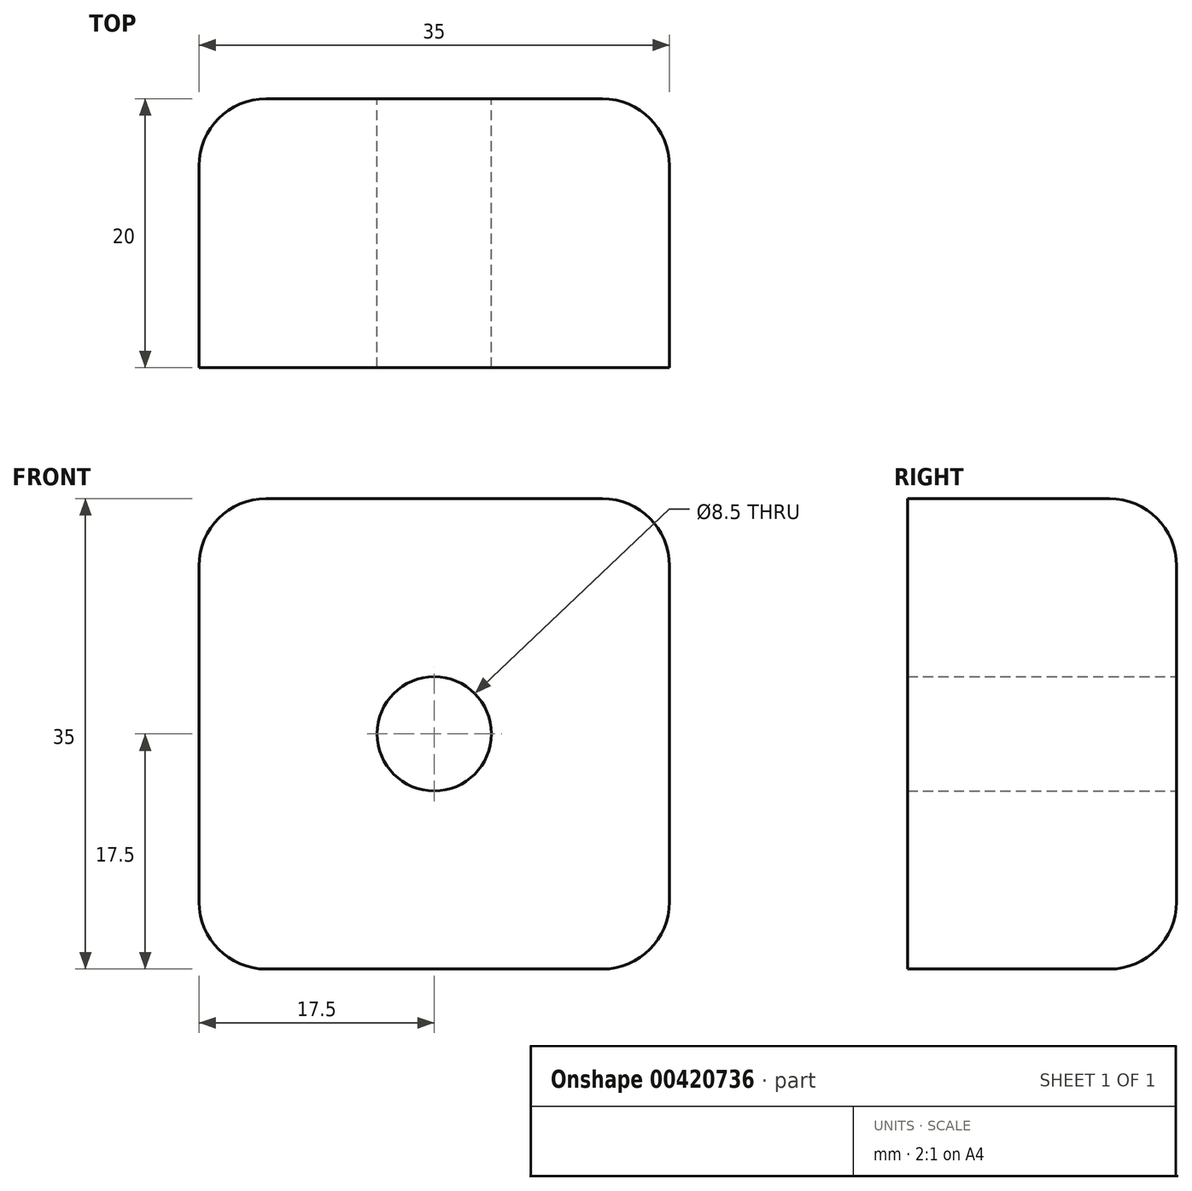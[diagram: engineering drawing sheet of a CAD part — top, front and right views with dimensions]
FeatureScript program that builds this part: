
annotation { "Feature Type Name" : "Feature", "Feature Type Description" : "" }
export const myFeature = defineFeature(function(context is Context, id is Id, definition is map)
    precondition{}
    {
        {
            var Q0;
            Q0=qCreatedBy(makeId("Front.planeOp"),FACE);
            var sketch = newSketch(context, id + "F0", { "sketchPlane" : qUnion([Q0])});
            skLineSegment(sketch, "E0", {"start": v(0, 0) * mm, "end": v(-35, 0) * mm});
            skLineSegment(sketch, "E1", {"start": v(-35, 0) * mm, "end": v(-35, 35) * mm});
            skLineSegment(sketch, "E2", {"start": v(-35, 35) * mm, "end": v(0, 35) * mm});
            skLineSegment(sketch, "E3", {"start": v(0, 35) * mm, "end": v(0, 0) * mm});
            skLineSegment(sketch, "E4", {"start": v(-17.5, 0) * mm, "end": v(-17.5, 17.5) * mm});
            skPoint(sketch, "E4.endSnap0", {"position": v(-35, 17.5) * mm});
            skCircle(sketch, "E5", {"center": v(-17.5, 17.5) * mm, "radius": 4.25 * mm});
            skSolve(sketch);
        }
        {
            var Q0;
            Q0 = qSketchRegion(id + "F0", true);
            var Q1;
            {var subQ0=sQuery(id+"F0.wireOp",EDGE,"E1");Q1=makeQuery(id+"F0.imprint","IMPRINT",FACE,{"disambiguationData":[TD([[makeQuery(id+"F0.imprint","IMPRINT",EDGE,{"derivedFrom":subQ0}),-1.0]])]});}
            extrude(context, id + "F1", {"entities" : qUnion([Q0, Q1]), "depth" : 20 * mm});
        }
        {
            var Q0;
            Q0=makeQuery(id+"F1.opExtrude","SWEPT_EDGE",EDGE,{"disambiguationData":[OSD([sQuery(id+"F0.wireOp",EDGE,"E1"),sQuery(id+"F0.wireOp",EDGE,"E2")])]});
            var Q1;
            Q1=makeQuery(id+"F1.opExtrude","SWEPT_EDGE",EDGE,{"disambiguationData":[OSD([sQuery(id+"F0.wireOp",EDGE,"E0"),sQuery(id+"F0.wireOp",EDGE,"E1")])]});
            var Q2;
            Q2=makeQuery(id+"F1.opExtrude","SWEPT_EDGE",EDGE,{"disambiguationData":[OSD([sQuery(id+"F0.wireOp",EDGE,"E2"),sQuery(id+"F0.wireOp",EDGE,"E3")])]});
            var Q3;
            Q3=makeQuery(id+"F1.opExtrude","SWEPT_EDGE",EDGE,{"disambiguationData":[OSD([sQuery(id+"F0.wireOp",EDGE,"E0"),sQuery(id+"F0.wireOp",EDGE,"E3")])]});
            var Q4;
            Q4=makeQuery(id+"F1.opExtrude","CAP_EDGE",EDGE,{"disambiguationData":[OSD([sQuery(id+"F0.wireOp",EDGE,"E2")])],"isStart":true});
            var Q5;
            Q5=makeQuery(id+"F1.opExtrude","CAP_EDGE",EDGE,{"disambiguationData":[OSD([sQuery(id+"F0.wireOp",EDGE,"E3")])],"isStart":true});
            var Q6;
            Q6=makeQuery(id+"F1.opExtrude","CAP_EDGE",EDGE,{"disambiguationData":[OSD([sQuery(id+"F0.wireOp",EDGE,"E0")])],"isStart":true});
            var Q7;
            Q7=makeQuery(id+"F1.opExtrude","CAP_EDGE",EDGE,{"disambiguationData":[OSD([sQuery(id+"F0.wireOp",EDGE,"E1")])],"isStart":true});
            fillet(context, id + "F2", {"entities" : qUnion([Q0, Q1, Q2, Q3, Q4, Q5, Q6, Q7]), "radius" : 5 * mm, "tangentPropagation" : true, "allowEdgeOverflow" : false});
        }
    });
